# Revit family: RN 90037 Optifitt-Serra-Verschlusszapfen
name_source: partatom
category: Rohrformteile
units: mm (PartAtom-declared; Revit-internal decimal feet)

## family parameters
Arbeitsebenenbasiert = Nein
Beim Laden mit Abzugskörper schneiden = Nein
Bemaßung runder Anschluss = Durchmesser verwenden
Gemeinsam genutzt = Nein
Immer vertikal = Ja
Teiletyp = Nicht definiert

## types (9) — shared parameters
1.010.00.2 Blattnummer der Richtlinie = 29
1.010.00.3 Ausgabedatum (Monat) der Richtlinie = 201308
1.010.00.4 Herstellername = R. Nussbaum AG
1.010.00.5 Revisionsdatum der Datei = 20190521
1.010.00.6 Webadresse des Herstellers = http://www.nussbaum.ch
1.100.00.4 Produktbezeichnung = Versorgung
1.110.00.2 Index = 3
1.110.00.4 Produktbezeichnung = Optifitt-Serra
1.960/3L.00.8 Link (URL) = https://www.nussbaum.ch
29.700.00.4 Produktname = Optifitt-Serra-Verschlusszapfen
29.700.00.5 Produktkennung = 2
29.700.00.6 Querschnittsform = 1
29.700.00.7 Nennweitensystem = DN
29.700.00.8 Nenndrucksystem = PN
29.710.02.4 Nenndruck = 16
29.710.02.5 max. zul. Überdruck [hPa] = 1600
29.710.02.7 max. zul. Dauer-Betriebsdruck [hPa] = 1600
29.710.02.9 max. zul. Dauer-Betriebstemperatur [°C] = 90
Connector Visibility = Nein
EnclosingSpace Visibility = Nein
Hersteller = R. Nussbaum AG
URL = https://www.nussbaum.ch

## per-type parameters (varying)
| type | 1.800.00.3 TGA-Nummer | 1.800.00.4 Kommentarfeld | 1.810.00.3 Hersteller-Bestellnummer | 1.810.00.4 DATANORM-Nummer | 1.810.00.5 StLB-Nummer | 1.810.00.6 GTIN-Nummer | 29.710.02.10 Formstück-Gewicht [kg] | 29.710.02.3 Benennung | CONNECTOR0_DIAMETER_dX_0r | CONNECTOR0_dX_01 | CONNECTOR0_ref_dX | Modell | R. Nussbaum AG 90037.02 de Visibility | R. Nussbaum AG 90037.03 de Visibility | R. Nussbaum AG 90037.04 de Visibility | R. Nussbaum AG 90037.05 de Visibility | R. Nussbaum AG 90037.06 de Visibility | R. Nussbaum AG 90037.07 de Visibility | R. Nussbaum AG 90037.08 de Visibility | R. Nussbaum AG 90037.09 de Visibility | R. Nussbaum AG 90037.10 de Visibility | Typenkommentare |
| DN=65 | 01900300000000000000000000000000000000000000000022000000000000000027 | 90037.10, Optifitt-Serra-Verschlusszapfen, DN=65, L=47, R=2½ | 90037.1 | 90037.1 | 216.118 | 7612945035028 | 0.422 | Optifitt-Serra-Verschlusszapfen, DN=65, L=47, R=2½ | 65 mm | 27 mm | 27 mm | 90037.1 | Nein | Nein | Nein | Nein | Nein | Nein | Nein | Nein | Ja | Optifitt-Serra-Verschlusszapfen  DN=65 |
| DN=50 | 01900300000000000000000000000000000000000000000022000000000000000008 | 90037.09, Optifitt-Serra-Verschlusszapfen, DN=50, L=42, R=2 | 90037.09 | 90037.09 | 216.117 | 7612945035011 | 0.337 | Optifitt-Serra-Verschlusszapfen, DN=50, L=42, R=2 | 50 mm | 24 mm | 24 mm | 90037.09 | Nein | Nein | Nein | Nein | Nein | Nein | Nein | Ja | Nein | Optifitt-Serra-Verschlusszapfen  DN=50 |
| DN=40 | 01900300000000000000000000000000000000000000000022000000000000000007 | 90037.08, Optifitt-Serra-Verschlusszapfen, DN=40, L=38, R=1½ | 90037.08 | 90037.08 | 216.116 | 7612945035004 | 0.186 | Optifitt-Serra-Verschlusszapfen, DN=40, L=38, R=1½ | 40 mm | 19 mm | 19 mm | 90037.08 | Nein | Nein | Nein | Nein | Nein | Nein | Ja | Nein | Nein | Optifitt-Serra-Verschlusszapfen  DN=40 |
| DN=32 | 01900300000000000000000000000000000000000000000022000000000000000006 | 90037.07, Optifitt-Serra-Verschlusszapfen, DN=32, L=38, R=1¼ | 90037.07 | 90037.07 | 216.115 | 7612945034991 | 0.157 | Optifitt-Serra-Verschlusszapfen, DN=32, L=38, R=1¼ | 32 mm | 19 mm | 19 mm | 90037.07 | Nein | Nein | Nein | Nein | Nein | Ja | Nein | Nein | Nein | Optifitt-Serra-Verschlusszapfen  DN=32 |
| DN=25 | 01900300000000000000000000000000000000000000000022000000000000000005 | 90037.06, Optifitt-Serra-Verschlusszapfen, DN=25, L=32, R=1 | 90037.06 | 90037.06 | 216.114 | 7612945034984 | 0.092 | Optifitt-Serra-Verschlusszapfen, DN=25, L=32, R=1 | 25 mm | 17 mm | 17 mm | 90037.06 | Nein | Nein | Nein | Nein | Ja | Nein | Nein | Nein | Nein | Optifitt-Serra-Verschlusszapfen  DN=25 |
| DN=20 | 01900300000000000000000000000000000000000000000022000000000000000004 | 90037.05, Optifitt-Serra-Verschlusszapfen, DN=20, L=28, R=¾ | 90037.05 | 90037.05 | 216.113 | 7612945034977 | 0.056 | Optifitt-Serra-Verschlusszapfen, DN=20, L=28, R=¾ | 20 mm | 15 mm | 15 mm | 90037.05 | Nein | Nein | Nein | Ja | Nein | Nein | Nein | Nein | Nein | Optifitt-Serra-Verschlusszapfen  DN=20 |
| DN=15 | 01900300000000000000000000000000000000000000000022000000000000000003 | 90037.04, Optifitt-Serra-Verschlusszapfen, DN=15, L=26, R=½ | 90037.04 | 90037.04 | 216.112 | 7612945034960 | 0.034 | Optifitt-Serra-Verschlusszapfen, DN=15, L=26, R=½ | 15 mm | 13 mm | 13 mm | 90037.04 | Nein | Nein | Ja | Nein | Nein | Nein | Nein | Nein | Nein | Optifitt-Serra-Verschlusszapfen  DN=15 |
| DN=1 | 01900300000000000000000000000000000000000000000022000000000000000002 | 90037.03, Optifitt-Serra-Verschlusszapfen, DN=10, L=20, R=3/8 | 90037.03 | 90037.03 | 216.111 | 7612945034953 | 0.021 | Optifitt-Serra-Verschlusszapfen, DN=10, L=20, R=3/8 | 10 mm  [stored 0.0328084 ft] | 10 mm  [stored 0.0328084 ft] | 10 mm  [stored 0.0328084 ft] | 90037.03 | Nein | Ja | Nein | Nein | Nein | Nein | Nein | Nein | Nein | Optifitt-Serra-Verschlusszapfen  DN=10 |
| DN=10 | 01900300000000000000000000000000000000000000000022000000000000000001 | 90037.02, Optifitt-Serra-Verschlusszapfen, DN=10, L=19, R=¼ | 90037.02 | 90037.02 |  | 7612945034946 | 0.012 | Optifitt-Serra-Verschlusszapfen, DN=10, L=19, R=¼ | 8 mm  [stored 0.0262467 ft] | 10 mm  [stored 0.0328084 ft] | 10 mm  [stored 0.0328084 ft] | 90037.02 | Ja | Nein | Nein | Nein | Nein | Nein | Nein | Nein | Nein | Optifitt-Serra-Verschlusszapfen  DN=10 |

note: [stored X ft] marks values corroborated as IEEE doubles in the binary element streams (Revit-internal decimal feet)

## geometry (parser evidence)
native form markers: Sweep x1
no freeform markers — native parametric forms only
